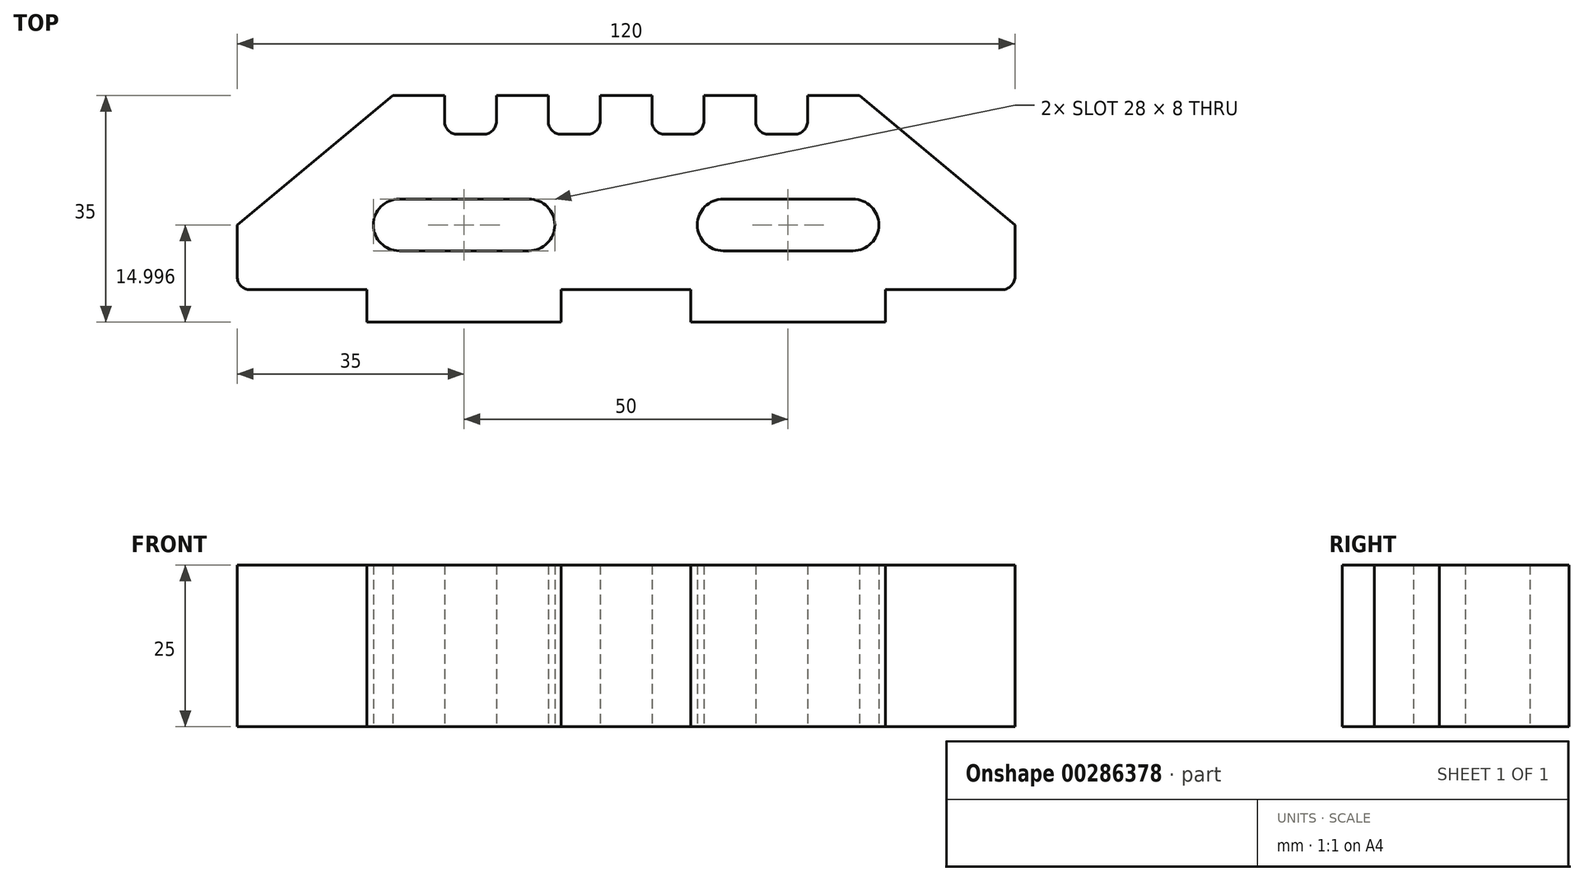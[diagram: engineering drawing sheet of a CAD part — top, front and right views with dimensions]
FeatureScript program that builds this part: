
annotation { "Feature Type Name" : "Feature", "Feature Type Description" : "" }
export const myFeature = defineFeature(function(context is Context, id is Id, definition is map)
    precondition{}
    {
        {
            var Q0;
            Q0=qCreatedBy(makeId("Top.planeOp"),FACE);
            var sketch = newSketch(context, id + "F0", { "sketchPlane" : qUnion([Q0])});
            skLineSegment(sketch, "E0", {"start": v(-68, -45.21) * mm, "end": v(-38, -45.21) * mm});
            skLineSegment(sketch, "E1", {"start": v(-38, -45.21) * mm, "end": v(-38, -40.21) * mm});
            skLineSegment(sketch, "E2", {"start": v(-38, -40.21) * mm, "end": v(-18, -40.21) * mm});
            skLineSegment(sketch, "E3", {"start": v(-18, -40.21) * mm, "end": v(-18, -45.21) * mm});
            skLineSegment(sketch, "E4", {"start": v(-18, -45.21) * mm, "end": v(12, -45.21) * mm});
            skLineSegment(sketch, "E5", {"start": v(-68, -45.21) * mm, "end": v(-68, -40.21) * mm});
            skLineSegment(sketch, "E6", {"start": v(12, -45.21) * mm, "end": v(12, -40.21) * mm});
            skLineSegment(sketch, "E7", {"start": v(12, -40.21) * mm, "end": v(30, -40.21) * mm});
            skLineSegment(sketch, "E8", {"start": v(-68, -40.21) * mm, "end": v(-86, -40.21) * mm});
            skLineSegment(sketch, "E9", {"start": v(-88, -38.21) * mm, "end": v(-88, -30.21) * mm});
            skLineSegment(sketch, "E10", {"start": v(-88, -30.21) * mm, "end": v(-64, -10.21) * mm});
            skLineSegment(sketch, "E11", {"start": v(-64, -10.21) * mm, "end": v(-56, -10.21) * mm});
            skLineSegment(sketch, "E12", {"start": v(-56, -10.21) * mm, "end": v(-56, -14.21) * mm});
            skLineSegment(sketch, "E13", {"start": v(-54, -16.21) * mm, "end": v(-50, -16.21) * mm});
            skLineSegment(sketch, "E14", {"start": v(-48, -14.21) * mm, "end": v(-48, -10.21) * mm});
            skLineSegment(sketch, "E15", {"start": v(-48, -10.21) * mm, "end": v(-40, -10.21) * mm});
            skLineSegment(sketch, "E16", {"start": v(-40, -10.21) * mm, "end": v(-40, -14.21) * mm});
            skLineSegment(sketch, "E17", {"start": v(-38, -16.21) * mm, "end": v(-34, -16.21) * mm});
            skLineSegment(sketch, "E18", {"start": v(-32, -14.21) * mm, "end": v(-32, -10.21) * mm});
            skLineSegment(sketch, "E19", {"start": v(-32, -10.21) * mm, "end": v(-24, -10.21) * mm});
            skLineSegment(sketch, "E20", {"start": v(-24, -10.21) * mm, "end": v(-24, -14.21) * mm});
            skLineSegment(sketch, "E21", {"start": v(-22, -16.21) * mm, "end": v(-18, -16.21) * mm});
            skLineSegment(sketch, "E22", {"start": v(-16, -14.21) * mm, "end": v(-16, -10.21) * mm});
            skLineSegment(sketch, "E23", {"start": v(-16, -10.21) * mm, "end": v(-8, -10.21) * mm});
            skLineSegment(sketch, "E24", {"start": v(-8, -10.21) * mm, "end": v(-8, -14.21) * mm});
            skLineSegment(sketch, "E25", {"start": v(-6, -16.21) * mm, "end": v(-2, -16.21) * mm});
            skLineSegment(sketch, "E26", {"start": v(0, -14.21) * mm, "end": v(0, -10.21) * mm});
            skLineSegment(sketch, "E27", {"start": v(0, -10.21) * mm, "end": v(8, -10.21) * mm});
            skLineSegment(sketch, "E28", {"start": v(32, -38.21) * mm, "end": v(32, -30.21) * mm});
            skLineSegment(sketch, "E29", {"start": v(8, -10.21) * mm, "end": v(32, -30.21) * mm});
            skPoint(sketch, "E30.visualSharp", {"position": v(-56, -16.21) * mm});
            skArc(sketch, "E30.filletArc", {"start": v(-56, -14.21) * mm, "mid": v(-55.41, -15.63) * mm, "end": v(-54, -16.21) * mm});
            skPoint(sketch, "E31.visualSharp", {"position": v(-48, -16.21) * mm});
            skArc(sketch, "E31.filletArc", {"start": v(-50, -16.21) * mm, "mid": v(-48.59, -15.63) * mm, "end": v(-48, -14.21) * mm});
            skPoint(sketch, "E32.visualSharp", {"position": v(-40, -16.21) * mm});
            skArc(sketch, "E32.filletArc", {"start": v(-40, -14.21) * mm, "mid": v(-39.41, -15.63) * mm, "end": v(-38, -16.21) * mm});
            skPoint(sketch, "E33.visualSharp", {"position": v(-32, -16.21) * mm});
            skArc(sketch, "E33.filletArc", {"start": v(-34, -16.21) * mm, "mid": v(-32.59, -15.63) * mm, "end": v(-32, -14.21) * mm});
            skPoint(sketch, "E34.visualSharp", {"position": v(-24, -16.21) * mm});
            skArc(sketch, "E34.filletArc", {"start": v(-24, -14.21) * mm, "mid": v(-23.41, -15.63) * mm, "end": v(-22, -16.21) * mm});
            skPoint(sketch, "E35.visualSharp", {"position": v(-16, -16.21) * mm});
            skArc(sketch, "E35.filletArc", {"start": v(-18, -16.21) * mm, "mid": v(-16.59, -15.63) * mm, "end": v(-16, -14.21) * mm});
            skPoint(sketch, "E36.visualSharp", {"position": v(-8, -16.21) * mm});
            skArc(sketch, "E36.filletArc", {"start": v(-8, -14.21) * mm, "mid": v(-7.41, -15.63) * mm, "end": v(-6, -16.21) * mm});
            skPoint(sketch, "E37.visualSharp", {"position": v(0, -16.21) * mm});
            skArc(sketch, "E37.filletArc", {"start": v(-2, -16.21) * mm, "mid": v(-0.59, -15.63) * mm, "end": v(0, -14.21) * mm});
            skLineSegment(sketch, "E38", {"start": v(-28, -40.21) * mm, "end": v(-28, -10.21) * mm});
            skPoint(sketch, "E39.start.orphan", {"position": v(-53, -45.21) * mm});
            skPoint(sketch, "E40.endSnap0", {"position": v(-17, -30.21) * mm});
            skLineSegment(sketch, "E41", {"start": v(-43, -26.21) * mm, "end": v(-63, -26.21) * mm});
            skLineSegment(sketch, "E42", {"start": v(-43, -34.21) * mm, "end": v(-63, -34.21) * mm});
            skLineSegment(sketch, "E43", {"start": v(-13, -34.21) * mm, "end": v(7, -34.21) * mm});
            skLineSegment(sketch, "E44", {"start": v(-13, -26.21) * mm, "end": v(7, -26.21) * mm});
            skArc(sketch, "E45", {"start": v(-63, -26.21) * mm, "mid": v(-67, -30.21) * mm, "end": v(-63, -34.21) * mm});
            skArc(sketch, "E46", {"start": v(-43, -34.21) * mm, "mid": v(-39, -30.21) * mm, "end": v(-43, -26.21) * mm});
            skArc(sketch, "E47", {"start": v(-13, -26.21) * mm, "mid": v(-17, -30.21) * mm, "end": v(-13, -34.21) * mm});
            skArc(sketch, "E48", {"start": v(7, -34.21) * mm, "mid": v(11, -30.21) * mm, "end": v(7, -26.21) * mm});
            skPoint(sketch, "E49.visualSharp", {"position": v(-88, -40.21) * mm});
            skArc(sketch, "E49.filletArc", {"start": v(-88, -38.21) * mm, "mid": v(-87.41, -39.63) * mm, "end": v(-86, -40.21) * mm});
            skPoint(sketch, "E50.visualSharp", {"position": v(32, -40.21) * mm});
            skArc(sketch, "E50.filletArc", {"start": v(30, -40.21) * mm, "mid": v(31.41, -39.63) * mm, "end": v(32, -38.21) * mm});
            skSolve(sketch);
        }
        {
            var Q0;
            Q0 = qSketchRegion(id + "F0", true);
            extrude(context, id + "F1", {"entities" : qUnion([Q0]), "depth" : 25 * mm});
        }
    });
